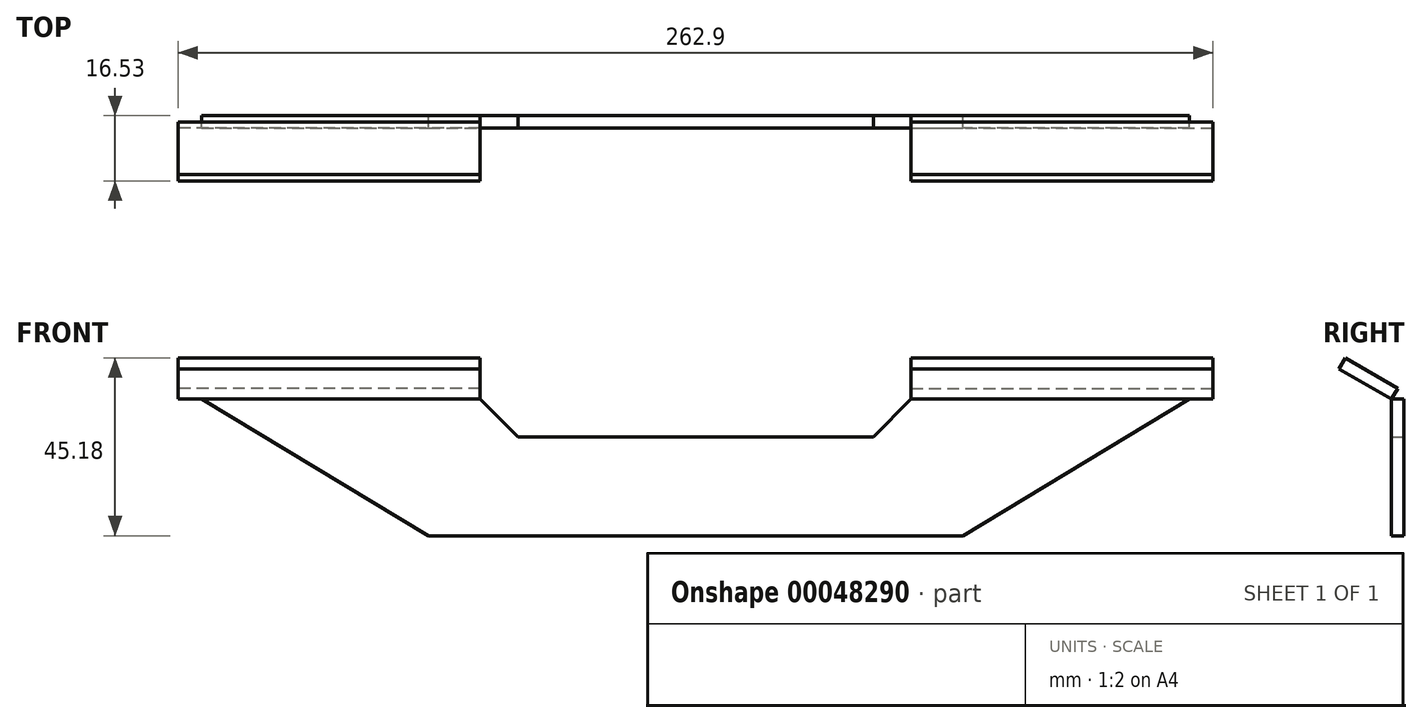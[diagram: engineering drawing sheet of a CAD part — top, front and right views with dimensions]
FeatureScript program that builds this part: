
annotation { "Feature Type Name" : "Feature", "Feature Type Description" : "" }
export const myFeature = defineFeature(function(context is Context, id is Id, definition is map)
    precondition{}
    {
        {
            var Q0;
            Q0=qCreatedBy(makeId("Front.planeOp"),FACE);
            var sketch = newSketch(context, id + "F0", { "sketchPlane" : qUnion([Q0])});
            skLineSegment(sketch, "E0", {"start": v(0, -13.43) * mm, "end": v(0, 11.7) * mm, "construction": true});
            skLineSegment(sketch, "E1", {"start": v(0, 11.7) * mm, "end": v(-45.14, 11.7) * mm});
            skLineSegment(sketch, "E2", {"start": v(-45.14, 11.7) * mm, "end": v(-54.73, 21.3) * mm});
            skLineSegment(sketch, "E3", {"start": v(-54.73, 21.3) * mm, "end": v(-125.5, 21.3) * mm});
            skLineSegment(sketch, "E4", {"start": v(-125.5, 21.3) * mm, "end": v(-67.88, -13.43) * mm});
            skLineSegment(sketch, "E5", {"start": v(-67.88, -13.43) * mm, "end": v(0, -13.43) * mm});
            skLineSegment(sketch, "E6.MirrorCS", {"start": v(125.5, 21.3) * mm, "end": v(67.88, -13.43) * mm});
            skLineSegment(sketch, "E7.MirrorCS", {"start": v(54.73, 21.3) * mm, "end": v(125.5, 21.3) * mm});
            skLineSegment(sketch, "E8.MirrorCS", {"start": v(45.14, 11.7) * mm, "end": v(54.73, 21.3) * mm});
            skLineSegment(sketch, "E9.MirrorCS", {"start": v(67.88, -13.43) * mm, "end": v(0, -13.43) * mm});
            skLineSegment(sketch, "E10.MirrorCS", {"start": v(0, 11.7) * mm, "end": v(45.14, 11.7) * mm});
            skSolve(sketch);
        }
        {
            var Q0;
            Q0 = qSketchRegion(id + "F0", true);
            extrude(context, id + "F1", {"entities" : qUnion([Q0]), "depth" : 3.17 * mm});
        }
        {
            var Q0;
            Q0=makeQuery(id+"F1.opExtrude","CAP_EDGE",EDGE,{"disambiguationData":[OSD([sQuery(id+"F0.wireOp",EDGE,"E3")])],"isStart":false});
            var Q1;
            Q1=qCreatedBy(makeId("Front.planeOp"),FACE);
            cPlane(context, id + "F2", {"entities" : qUnion([Q0, Q1]), "cplaneType" : CPlaneType.LINE_ANGLE, "offset" : 25.4 * mm, "angle" : 120 * degree, "width" : 152.4 * mm, "height" : 152.4 * mm});
        }
        {
            var Q0;
            Q0=qCreatedBy(id+"F2.planeOp",FACE);
            var sketch = newSketch(context, id + "F3", { "sketchPlane" : qUnion([Q0])});
            skLineSegment(sketch, "E11.0", {"start": v(-54.73, 13.4) * mm, "end": v(-125.5, 13.4) * mm, "construction": true});
            skLineSegment(sketch, "E12.bottom", {"start": v(-54.73, 13.4) * mm, "end": v(-131.45, 13.4) * mm});
            skLineSegment(sketch, "E12.top", {"start": v(-54.73, 28.82) * mm, "end": v(-131.45, 28.82) * mm});
            skLineSegment(sketch, "E12.left", {"start": v(-54.73, 13.4) * mm, "end": v(-54.73, 28.82) * mm});
            skLineSegment(sketch, "E12.right", {"start": v(-131.45, 13.4) * mm, "end": v(-131.45, 28.82) * mm});
            skSolve(sketch);
        }
        {
            var Q0;
            Q0 = qSketchRegion(id + "F3", true);
            extrude(context, id + "F4", {"entities" : qUnion([Q0]), "oppositeDirection" : true, "depth" : 3.17 * mm});
        }
        {
            var Q0;
            Q0=makeQuery(id+"F4.opExtrude","SWEPT_BODY",BODY,{"disambiguationData":[OSD([sQuery(id+"F3.wireOp",EDGE,"E12.bottom"),sQuery(id+"F3.wireOp",EDGE,"E12.top"),sQuery(id+"F3.wireOp",EDGE,"E12.left"),sQuery(id+"F3.wireOp",EDGE,"E12.right")])]});
            var Q1;
            Q1=qCreatedBy(makeId("Right.planeOp"),FACE);
            mirror(context, id + "F5", {"entities" : qUnion([Q0]), "mirrorPlane" : qUnion([Q1])});
        }
    });
